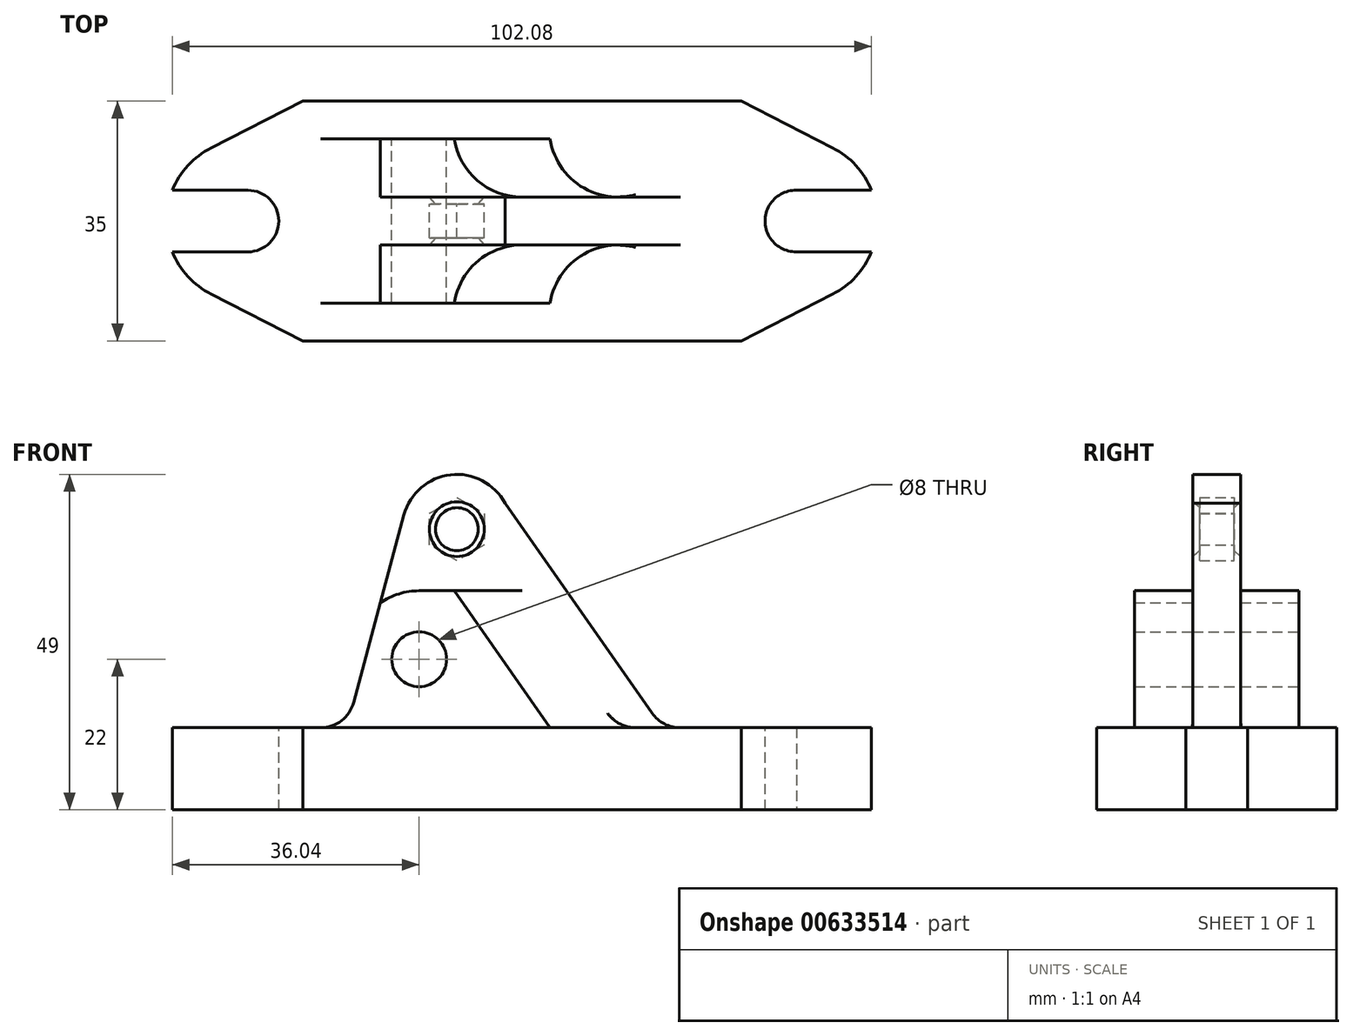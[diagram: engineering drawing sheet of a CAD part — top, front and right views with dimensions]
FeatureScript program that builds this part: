
annotation { "Feature Type Name" : "Feature", "Feature Type Description" : "" }
export const myFeature = defineFeature(function(context is Context, id is Id, definition is map)
    precondition{}
    {
        {
            var Q0;
            Q0=qCreatedBy(makeId("Front.planeOp"),FACE);
            var sketch = newSketch(context, id + "F0", { "sketchPlane" : qUnion([Q0])});
            skLineSegment(sketch, "E0.bottom", {"start": v(52, 6) * mm, "end": v(23.1, 6) * mm});
            skLineSegment(sketch, "E0.top", {"start": v(52, -6) * mm, "end": v(-52, -6) * mm});
            skLineSegment(sketch, "E0.left", {"start": v(-52, 6) * mm, "end": v(-52, -6) * mm});
            skLineSegment(sketch, "E0.right", {"start": v(52, 6) * mm, "end": v(52, -6) * mm});
            skPoint(sketch, "E0.middle", {"position": v(0, 0) * mm});
            skCircle(sketch, "E1", {"center": v(-9.5, 35) * mm, "radius": 2.75 * mm});
            skArc(sketch, "E2", {"start": v(-17.23, 37.07) * mm, "mid": v(-10.42, 42.95) * mm, "end": v(-2.45, 38.78) * mm});
            skLineSegment(sketch, "E3", {"start": v(-17.23, 37.07) * mm, "end": v(-24.56, 9.7) * mm});
            skLineSegment(sketch, "E4", {"start": v(-2.45, 38.78) * mm, "end": v(19.01, 8.13) * mm});
            skLineSegment(sketch, "E5", {"start": v(-9.5, 35) * mm, "end": v(-9.5, 6) * mm});
            skCircle(sketch, "E6", {"center": v(-15, 16) * mm, "radius": 4 * mm});
            skPoint(sketch, "E7.newPointB", {"position": v(-52, 6) * mm});
            skArc(sketch, "E7.filletArc", {"start": v(19.01, 8.13) * mm, "mid": v(20.8, 6.56) * mm, "end": v(23.1, 6) * mm});
            skLineSegment(sketch, "E8", {"start": v(-29.39, 6) * mm, "end": v(-52, 6) * mm});
            skPoint(sketch, "E9.visualSharp", {"position": v(-25.55, 6) * mm});
            skArc(sketch, "E9.filletArc", {"start": v(-29.39, 6) * mm, "mid": v(-26.35, 7.03) * mm, "end": v(-24.56, 9.7) * mm});
            skLineSegment(sketch, "E10", {"start": v(16.6, 6) * mm, "end": v(23.1, 6) * mm});
            skLineSegment(sketch, "E11", {"start": v(-9.5, 26) * mm, "end": v(3.01, 8.13) * mm});
            skArc(sketch, "E12.filletArc", {"start": v(3.01, 8.13) * mm, "mid": v(4.8, 6.56) * mm, "end": v(7.1, 6) * mm});
            skLineSegment(sketch, "E13", {"start": v(-29.39, 6) * mm, "end": v(9.04, 6) * mm});
            skLineSegment(sketch, "E14", {"start": v(-15, 16) * mm, "end": v(-15, 26) * mm});
            skLineSegment(sketch, "E15", {"start": v(-15, 26) * mm, "end": v(-9.5, 26) * mm});
            skArc(sketch, "E16", {"start": v(-15, 26) * mm, "mid": v(-17.97, 25.55) * mm, "end": v(-20.67, 24.24) * mm});
            skLineSegment(sketch, "E17", {"start": v(-15, 26) * mm, "end": v(0, 26) * mm});
            skLineSegment(sketch, "E18", {"start": v(0, 26) * mm, "end": v(12.51, 8.13) * mm});
            skArc(sketch, "E19.filletArc", {"start": v(12.51, 8.13) * mm, "mid": v(14.3, 6.56) * mm, "end": v(16.6, 6) * mm});
            skLineSegment(sketch, "E20", {"start": v(7.1, 6) * mm, "end": v(16.6, 6) * mm});
            skSolve(sketch);
        }
        {
            var Q0;
            Q0=makeQuery(id+"F0.imprint","IMPRINT",FACE,{"disambiguationData":[TD([[makeQuery(id+"F0.imprint","IMPRINT",EDGE,{"derivedFrom":sQuery(id+"F0.wireOp",EDGE,"E0.bottom")}),1.0]])]});
            extrude(context, id + "F1", {"entities" : qUnion([Q0]), "endBound" : BoundingType.SYMMETRIC, "depth" : 35 * mm, "offsetDistance" : 25 * mm});
        }
        {
            var Q0;
            Q0=makeQuery(id+"F0.imprint","IMPRINT",FACE,{"disambiguationData":[TD([[makeQuery(id+"F0.imprint","IMPRINT",EDGE,{"derivedFrom":sQuery(id+"F0.wireOp",EDGE,"E6")}),-1.0]])]});
            var Q1;
            {var subQ3=sQuery(id+"F0.wireOp",EDGE,"E11");Q1=makeQuery(id+"F0.imprint","IMPRINT",FACE,{"disambiguationData":[TD([[makeQuery(id+"F0.imprint","IMPRINT",EDGE,{"derivedFrom":subQ3}),-1.0]])]});}
            var Q2;
            {var subQ2=sQuery(id+"F0.wireOp",EDGE,"E11");Q2=makeQuery(id+"F0.imprint","IMPRINT",FACE,{"disambiguationData":[TD([[makeQuery(id+"F0.imprint","IMPRINT",EDGE,{"derivedFrom":subQ2}),1.0]])]});}
            extrude(context, id + "F2", {"entities" : qUnion([Q0, Q1, Q2]), "operationType" : NewBodyOperationType.ADD, "endBound" : BoundingType.SYMMETRIC, "depth" : 24 * mm, "offsetDistance" : 25 * mm});
        }
        {
            var Q0;
            Q0=makeQuery(id+"F0.imprint","IMPRINT",FACE,{"disambiguationData":[TD([[makeQuery(id+"F0.imprint","IMPRINT",EDGE,{"derivedFrom":sQuery(id+"F0.wireOp",EDGE,"E1")}),-1.0]])]});
            extrude(context, id + "F3", {"entities" : qUnion([Q0]), "operationType" : NewBodyOperationType.ADD, "endBound" : BoundingType.SYMMETRIC, "depth" : 7 * mm, "offsetDistance" : 25 * mm});
        }
        {
            var Q0;
            {var subQ0=sQuery(id+"F0.wireOp",EDGE,"E19.filletArc");var subQ1=sQuery(id+"F0.wireOp",EDGE,"E18");var subQ2=sQuery(id+"F0.wireOp",EDGE,"E17");var subQ3=sQuery(id+"F0.wireOp",EDGE,"E16");var subQ4=sQuery(id+"F0.wireOp",EDGE,"E3");Q0=makeQuery(id+"F3.boolean.opBoolean","SPLIT",FACE,{"disambiguationData":[TD([makeQuery(id+"F2.opExtrude","CAP_FACE",FACE,{"disambiguationData":[OSD([subQ4,sQuery(id+"F0.wireOp",EDGE,"E6"),sQuery(id+"F0.wireOp",EDGE,"E9.filletArc"),sQuery(id+"F0.wireOp",EDGE,"E13"),subQ3,subQ2,subQ1,subQ0,sQuery(id+"F0.wireOp",EDGE,"E20")])],"isStart":false})])],"derivedFrom":makeQuery(id+"F2.opExtrude","SWEPT_FACE",FACE,{"disambiguationData":[OSD([subQ2])]})});}
            var sketch = newSketch(context, id + "F4", { "sketchPlane" : qUnion([Q0])});
            skCircle(sketch, "E21", {"center": v(0, -13.5) * mm, "radius": 10 * mm});
            skSolve(sketch);
        }
        {
            var Q0;
            Q0=makeQuery(id+"F2.opExtrude","CAP_FACE",FACE,{"disambiguationData":[OSD([sQuery(id+"F0.wireOp",EDGE,"E3"),sQuery(id+"F0.wireOp",EDGE,"E6"),sQuery(id+"F0.wireOp",EDGE,"E9.filletArc"),sQuery(id+"F0.wireOp",EDGE,"E13"),sQuery(id+"F0.wireOp",EDGE,"E16"),sQuery(id+"F0.wireOp",EDGE,"E17"),sQuery(id+"F0.wireOp",EDGE,"E18"),sQuery(id+"F0.wireOp",EDGE,"E19.filletArc"),sQuery(id+"F0.wireOp",EDGE,"E20")])],"isStart":false});
            var sketch = newSketch(context, id + "F5", { "sketchPlane" : qUnion([Q0])});
            skLineSegment(sketch, "E22", {"start": v(0, 26) * mm, "end": v(14, 6) * mm});
            skSolve(sketch);
        }
        {
            var Q0;
            Q0=makeQuery(id+"F2.opExtrude","CAP_FACE",FACE,{"disambiguationData":[OSD([sQuery(id+"F0.wireOp",EDGE,"E3"),sQuery(id+"F0.wireOp",EDGE,"E6"),sQuery(id+"F0.wireOp",EDGE,"E9.filletArc"),sQuery(id+"F0.wireOp",EDGE,"E13"),sQuery(id+"F0.wireOp",EDGE,"E16"),sQuery(id+"F0.wireOp",EDGE,"E17"),sQuery(id+"F0.wireOp",EDGE,"E18"),sQuery(id+"F0.wireOp",EDGE,"E19.filletArc"),sQuery(id+"F0.wireOp",EDGE,"E20")])],"isStart":true});
            var sketch = newSketch(context, id + "F6", { "sketchPlane" : qUnion([Q0])});
            skLineSegment(sketch, "E23", {"start": v(0, 26) * mm, "end": v(-14, 6) * mm});
            skSolve(sketch);
        }
        {
            var Q0;
            {var subQ0=sQuery(id+"F0.wireOp",EDGE,"E19.filletArc");var subQ1=sQuery(id+"F0.wireOp",EDGE,"E18");var subQ2=sQuery(id+"F0.wireOp",EDGE,"E17");var subQ3=sQuery(id+"F0.wireOp",EDGE,"E16");var subQ4=sQuery(id+"F0.wireOp",EDGE,"E3");Q0=makeQuery(id+"F3.boolean.opBoolean","SPLIT",FACE,{"disambiguationData":[TD([makeQuery(id+"F2.opExtrude","CAP_FACE",FACE,{"disambiguationData":[OSD([subQ4,sQuery(id+"F0.wireOp",EDGE,"E6"),sQuery(id+"F0.wireOp",EDGE,"E9.filletArc"),sQuery(id+"F0.wireOp",EDGE,"E13"),subQ3,subQ2,subQ1,subQ0,sQuery(id+"F0.wireOp",EDGE,"E20")])],"isStart":true})])],"derivedFrom":makeQuery(id+"F2.opExtrude","SWEPT_FACE",FACE,{"disambiguationData":[OSD([subQ2])]})});}
            var sketch = newSketch(context, id + "F7", { "sketchPlane" : qUnion([Q0])});
            skCircle(sketch, "E24", {"center": v(0, 13.5) * mm, "radius": 10 * mm});
            skSolve(sketch);
        }
        {
            var Q0;
            Q0=qSketchRegion(id+"F4",true);
            var Q1;
            Q1=sQuery(id+"F5.wireOp",EDGE,"E22");
            sweep(context, id + "F8", {"operationType" : NewBodyOperationType.REMOVE, "profiles" : qUnion([Q0]), "path" : qUnion([Q1])});
        }
        {
            var Q0;
            Q0=qSketchRegion(id+"F7",true);
            var Q1;
            Q1=sQuery(id+"F6.wireOp",EDGE,"E23");
            sweep(context, id + "F9", {"operationType" : NewBodyOperationType.REMOVE, "profiles" : qUnion([Q0]), "path" : qUnion([Q1])});
        }
        {
            var Q0;
            Q0=makeQuery(id+"F9.boolean.opBoolean","MERGE",FACE,{"derivedFrom":[makeQuery(id+"F8.boolean.opBoolean","MERGE",FACE,{"derivedFrom":[makeQuery(id+"F1.opExtrude","SWEPT_FACE",FACE,{"disambiguationData":[OSD([sQuery(id+"F0.wireOp",EDGE,"E0.bottom"),sQuery(id+"F0.wireOp",EDGE,"E8"),sQuery(id+"F0.wireOp",EDGE,"E10"),sQuery(id+"F0.wireOp",EDGE,"E13"),sQuery(id+"F0.wireOp",EDGE,"E20")])]}),makeQuery(id+"F8.opSweep","CAP_FACE",FACE,{"disambiguationData":[OSD([sQuery(id+"F4.wireOp",EDGE,"E21"),sQuery(id+"F5.wireOp",VERTEX,"E22.end")])],"isStart":false})]}),makeQuery(id+"F9.opSweep","CAP_FACE",FACE,{"disambiguationData":[OSD([sQuery(id+"F6.wireOp",VERTEX,"E23.end"),sQuery(id+"F7.wireOp",EDGE,"E24")])],"isStart":false})]});
            var sketch = newSketch(context, id + "F10", { "sketchPlane" : qUnion([Q0])});
            skCircle(sketch, "E25", {"center": v(40, 0) * mm, "radius": 4.5 * mm});
            skSolve(sketch);
        }
        {
            var Q0;
            Q0=sQuery(id+"F10.wireOp",VERTEX,"E25.center");
            var Q1;
            Q1=makeQuery(id+"F1.opExtrude","SWEPT_BODY",BODY,{"disambiguationData":[OSD([sQuery(id+"F0.wireOp",EDGE,"E0.bottom"),sQuery(id+"F0.wireOp",EDGE,"E0.top"),sQuery(id+"F0.wireOp",EDGE,"E0.left"),sQuery(id+"F0.wireOp",EDGE,"E0.right"),sQuery(id+"F0.wireOp",EDGE,"E8"),sQuery(id+"F0.wireOp",EDGE,"E10"),sQuery(id+"F0.wireOp",EDGE,"E13"),sQuery(id+"F0.wireOp",EDGE,"E20")])]});
            hole(context, id + "F11", {"style" : HoleStyle.SIMPLE, "endStyle" : HoleEndStyle.THROUGH, "holeDiameter" : 9 * mm, "isTappedThrough" : true, "tappedDepth" : 12 * mm, "tapClearance" : 3, "startFromSketch" : true, "locations" : qUnion([Q0]), "scope" : qUnion([Q1])});
        }
        {
            var Q0;
            Q0=makeQuery(id+"F9.boolean.opBoolean","MERGE",FACE,{"derivedFrom":[makeQuery(id+"F8.boolean.opBoolean","MERGE",FACE,{"derivedFrom":[makeQuery(id+"F1.opExtrude","SWEPT_FACE",FACE,{"disambiguationData":[OSD([sQuery(id+"F0.wireOp",EDGE,"E0.bottom"),sQuery(id+"F0.wireOp",EDGE,"E8"),sQuery(id+"F0.wireOp",EDGE,"E10"),sQuery(id+"F0.wireOp",EDGE,"E13"),sQuery(id+"F0.wireOp",EDGE,"E20")])]}),makeQuery(id+"F8.opSweep","CAP_FACE",FACE,{"disambiguationData":[OSD([sQuery(id+"F4.wireOp",EDGE,"E21"),sQuery(id+"F5.wireOp",VERTEX,"E22.end")])],"isStart":false})]}),makeQuery(id+"F9.opSweep","CAP_FACE",FACE,{"disambiguationData":[OSD([sQuery(id+"F6.wireOp",VERTEX,"E23.end"),sQuery(id+"F7.wireOp",EDGE,"E24")])],"isStart":false})]});
            var sketch = newSketch(context, id + "F12", { "sketchPlane" : qUnion([Q0])});
            skCircle(sketch, "E26", {"center": v(-40, 0) * mm, "radius": 4.5 * mm});
            skLineSegment(sketch, "E27", {"start": v(-40, 4.5) * mm, "end": v(-52, 4.5) * mm});
            skLineSegment(sketch, "E28", {"start": v(-40, -4.5) * mm, "end": v(-52, -4.5) * mm});
            skLineSegment(sketch, "E29", {"start": v(32, -17.5) * mm, "end": v(32, 17.5) * mm});
            skLineSegment(sketch, "E30", {"start": v(32, -17.5) * mm, "end": v(45.36, -10.7) * mm});
            skLineSegment(sketch, "E31", {"start": v(45.36, 10.7) * mm, "end": v(32, 17.5) * mm});
            skPoint(sketch, "E32.visualSharp", {"position": v(66.35, 0) * mm});
            skArc(sketch, "E32.filletArc", {"start": v(45.36, -10.7) * mm, "mid": v(51.91, 0) * mm, "end": v(45.36, 10.7) * mm});
            skLineSegment(sketch, "E33", {"start": v(39.91, -4.5) * mm, "end": v(52, -4.5) * mm});
            skLineSegment(sketch, "E34", {"start": v(39.91, 4.5) * mm, "end": v(52, 4.5) * mm});
            skSolve(sketch);
        }
        {
            var Q0;
            Q0=sQuery(id+"F12.wireOp",VERTEX,"E26.center");
            var Q1;
            Q1=makeQuery(id+"F1.opExtrude","SWEPT_BODY",BODY,{"disambiguationData":[OSD([sQuery(id+"F0.wireOp",EDGE,"E0.bottom"),sQuery(id+"F0.wireOp",EDGE,"E0.top"),sQuery(id+"F0.wireOp",EDGE,"E0.left"),sQuery(id+"F0.wireOp",EDGE,"E0.right"),sQuery(id+"F0.wireOp",EDGE,"E8"),sQuery(id+"F0.wireOp",EDGE,"E10"),sQuery(id+"F0.wireOp",EDGE,"E13"),sQuery(id+"F0.wireOp",EDGE,"E20")])]});
            hole(context, id + "F13", {"style" : HoleStyle.SIMPLE, "endStyle" : HoleEndStyle.THROUGH, "holeDiameter" : 9 * mm, "isTappedThrough" : true, "tappedDepth" : 12 * mm, "tapClearance" : 3, "startFromSketch" : true, "locations" : qUnion([Q0]), "scope" : qUnion([Q1])});
        }
        {
            var Q0;
            Q0=makeQuery(id+"F9.boolean.opBoolean","MERGE",FACE,{"derivedFrom":[makeQuery(id+"F8.boolean.opBoolean","MERGE",FACE,{"derivedFrom":[makeQuery(id+"F1.opExtrude","SWEPT_FACE",FACE,{"disambiguationData":[OSD([sQuery(id+"F0.wireOp",EDGE,"E0.bottom"),sQuery(id+"F0.wireOp",EDGE,"E8"),sQuery(id+"F0.wireOp",EDGE,"E10"),sQuery(id+"F0.wireOp",EDGE,"E13"),sQuery(id+"F0.wireOp",EDGE,"E20")])]}),makeQuery(id+"F8.opSweep","CAP_FACE",FACE,{"disambiguationData":[OSD([sQuery(id+"F4.wireOp",EDGE,"E21"),sQuery(id+"F5.wireOp",VERTEX,"E22.end")])],"isStart":false})]}),makeQuery(id+"F9.opSweep","CAP_FACE",FACE,{"disambiguationData":[OSD([sQuery(id+"F6.wireOp",VERTEX,"E23.end"),sQuery(id+"F7.wireOp",EDGE,"E24")])],"isStart":false})]});
            var sketch = newSketch(context, id + "F14", { "sketchPlane" : qUnion([Q0])});
            skLineSegment(sketch, "E35", {"start": v(-32, 17.5) * mm, "end": v(-32, -17.5) * mm});
            skLineSegment(sketch, "E36", {"start": v(-32, 17.5) * mm, "end": v(-45.36, 10.7) * mm});
            skPoint(sketch, "E36.endSnap0", {"position": v(-52, 0) * mm});
            skLineSegment(sketch, "E37", {"start": v(-45.36, -10.7) * mm, "end": v(-32, -17.5) * mm});
            skPoint(sketch, "E38.visualSharp", {"position": v(-66.35, 0) * mm});
            skArc(sketch, "E38.filletArc", {"start": v(-45.36, 10.7) * mm, "mid": v(-51.91, 0) * mm, "end": v(-45.36, -10.7) * mm});
            skSolve(sketch);
        }
        {
            var Q0;
            {var subQ3=sQuery(id+"F14.wireOp",EDGE,"E36");Q0=makeQuery(id+"F14.imprint","IMPRINT",FACE,{"disambiguationData":[TD([[makeQuery(id+"F14.imprint","IMPRINT",EDGE,{"derivedFrom":subQ3}),-1.0]])]});}
            var Q1;
            Q1=makeQuery(id+"F1.opExtrude","CAP_EDGE",EDGE,{"disambiguationData":[OSD([sQuery(id+"F0.wireOp",EDGE,"E0.left")])],"isStart":false});
            sweep(context, id + "F15", {"operationType" : NewBodyOperationType.REMOVE, "profiles" : qUnion([Q0]), "path" : qUnion([Q1])});
        }
        {
            var Q0;
            {var subQ0=sQuery(id+"F12.wireOp",EDGE,"E27");Q0=makeQuery(id+"F12.imprint","IMPRINT",FACE,{"disambiguationData":[TD([[makeQuery(id+"F12.imprint","IMPRINT",EDGE,{"derivedFrom":subQ0}),1.0]])]});}
            var Q1;
            Q1=sQuery(id+"F0.wireOp",EDGE,"E0.left");
            sweep(context, id + "F16", {"operationType" : NewBodyOperationType.REMOVE, "profiles" : qUnion([Q0]), "path" : qUnion([Q1])});
        }
        {
            var Q0;
            {var subQ3=sQuery(id+"F12.wireOp",EDGE,"E30");Q0=makeQuery(id+"F12.imprint","IMPRINT",FACE,{"disambiguationData":[TD([[makeQuery(id+"F12.imprint","IMPRINT",EDGE,{"derivedFrom":subQ3}),-1.0]])]});}
            var Q1;
            Q1=makeQuery(id+"F1.opExtrude","CAP_EDGE",EDGE,{"disambiguationData":[OSD([sQuery(id+"F0.wireOp",EDGE,"E0.right")])],"isStart":true});
            sweep(context, id + "F17", {"operationType" : NewBodyOperationType.REMOVE, "profiles" : qUnion([Q0]), "path" : qUnion([Q1])});
        }
        {
            var Q0;
            {var subQ0=sQuery(id+"F12.wireOp",EDGE,"E33");var subQ1=sQuery(id+"F12.wireOp",EDGE,"E32.filletArc");var subQ2=makeQuery(id+"F12.imprint","INTERSECT",VERTEX,{"derivedFrom":[subQ1,subQ0]});Q0=makeQuery(id+"F12.imprint","IMPRINT",FACE,{"disambiguationData":[TD([[makeQuery(id+"F12.imprint","IMPRINT",EDGE,{"disambiguationData":[TD([[subQ2,-1.0]])],"derivedFrom":subQ1}),1.0]])]});}
            var Q1;
            {var subQ0=sQuery(id+"F12.wireOp",EDGE,"E33");var subQ1=sQuery(id+"F12.wireOp",EDGE,"E32.filletArc");var subQ2=makeQuery(id+"F12.imprint","INTERSECT",VERTEX,{"derivedFrom":[subQ1,subQ0]});Q1=makeQuery(id+"F12.imprint","IMPRINT",FACE,{"disambiguationData":[TD([[makeQuery(id+"F12.imprint","IMPRINT",EDGE,{"disambiguationData":[TD([[subQ2,-1.0]])],"derivedFrom":subQ1}),-1.0]])]});}
            var Q2;
            {var subQ8=sQuery(id+"F12.wireOp",EDGE,"E31");Q2=makeQuery(id+"F12.imprint","IMPRINT",FACE,{"disambiguationData":[TD([[makeQuery(id+"F12.imprint","IMPRINT",EDGE,{"derivedFrom":subQ8}),-1.0]])]});}
            var Q3;
            Q3=makeQuery(id+"F1.opExtrude","CAP_EDGE",EDGE,{"disambiguationData":[OSD([sQuery(id+"F0.wireOp",EDGE,"E0.right")])],"isStart":true});
            sweep(context, id + "F18", {"operationType" : NewBodyOperationType.REMOVE, "profiles" : qUnion([Q0, Q1, Q2]), "path" : qUnion([Q3])});
        }
        {
            var Q0;
            Q0=makeQuery(id+"F3.opExtrude","CAP_FACE",FACE,{"disambiguationData":[OSD([sQuery(id+"F0.wireOp",EDGE,"E1"),sQuery(id+"F0.wireOp",EDGE,"E2"),sQuery(id+"F0.wireOp",EDGE,"E3"),sQuery(id+"F0.wireOp",EDGE,"E4"),sQuery(id+"F0.wireOp",EDGE,"E7.filletArc"),sQuery(id+"F0.wireOp",EDGE,"E10"),sQuery(id+"F0.wireOp",EDGE,"E16"),sQuery(id+"F0.wireOp",EDGE,"E17"),sQuery(id+"F0.wireOp",EDGE,"E18"),sQuery(id+"F0.wireOp",EDGE,"E19.filletArc")])],"isStart":false});
            var sketch = newSketch(context, id + "F19", { "sketchPlane" : qUnion([Q0])});
            skPoint(sketch, "E39", {"position": v(-9.5, 35) * mm});
            skSolve(sketch);
        }
        {
            var Q0;
            Q0=sQuery(id+"F19.wireOp",VERTEX,"E39");
            var Q1;
            Q1=makeQuery(id+"F1.opExtrude","SWEPT_BODY",BODY,{"disambiguationData":[OSD([sQuery(id+"F0.wireOp",EDGE,"E0.bottom"),sQuery(id+"F0.wireOp",EDGE,"E0.top"),sQuery(id+"F0.wireOp",EDGE,"E0.left"),sQuery(id+"F0.wireOp",EDGE,"E0.right"),sQuery(id+"F0.wireOp",EDGE,"E8"),sQuery(id+"F0.wireOp",EDGE,"E10"),sQuery(id+"F0.wireOp",EDGE,"E13"),sQuery(id+"F0.wireOp",EDGE,"E20")])]});
            hole(context, id + "F20", {"style" : HoleStyle.C_SINK, "endStyle" : HoleEndStyle.BLIND, "holeDiameter" : 5.5 * mm, "cSinkDiameter" : 8 * mm, "cSinkAngle" : 82 * degree, "holeDepth" : 3.5 * mm, "isTappedThrough" : true, "tappedDepth" : 12 * mm, "tapClearance" : 3, "startFromSketch" : true, "locations" : qUnion([Q0]), "scope" : qUnion([Q1])});
        }
        {
            var Q0;
            Q0=makeQuery(id+"F3.opExtrude","CAP_FACE",FACE,{"disambiguationData":[OSD([sQuery(id+"F0.wireOp",EDGE,"E1"),sQuery(id+"F0.wireOp",EDGE,"E2"),sQuery(id+"F0.wireOp",EDGE,"E3"),sQuery(id+"F0.wireOp",EDGE,"E4"),sQuery(id+"F0.wireOp",EDGE,"E7.filletArc"),sQuery(id+"F0.wireOp",EDGE,"E10"),sQuery(id+"F0.wireOp",EDGE,"E16"),sQuery(id+"F0.wireOp",EDGE,"E17"),sQuery(id+"F0.wireOp",EDGE,"E18"),sQuery(id+"F0.wireOp",EDGE,"E19.filletArc")])],"isStart":true});
            var sketch = newSketch(context, id + "F21", { "sketchPlane" : qUnion([Q0])});
            skPoint(sketch, "E40", {"position": v(9.5, 35) * mm});
            skSolve(sketch);
        }
        {
            var Q0;
            Q0=sQuery(id+"F21.wireOp",VERTEX,"E40");
            var Q1;
            Q1=makeQuery(id+"F1.opExtrude","SWEPT_BODY",BODY,{"disambiguationData":[OSD([sQuery(id+"F0.wireOp",EDGE,"E0.bottom"),sQuery(id+"F0.wireOp",EDGE,"E0.top"),sQuery(id+"F0.wireOp",EDGE,"E0.left"),sQuery(id+"F0.wireOp",EDGE,"E0.right"),sQuery(id+"F0.wireOp",EDGE,"E8"),sQuery(id+"F0.wireOp",EDGE,"E10"),sQuery(id+"F0.wireOp",EDGE,"E13"),sQuery(id+"F0.wireOp",EDGE,"E20")])]});
            hole(context, id + "F22", {"style" : HoleStyle.C_SINK, "endStyle" : HoleEndStyle.BLIND, "holeDiameter" : 5.5 * mm, "cSinkDiameter" : 8 * mm, "cSinkAngle" : 82 * degree, "holeDepth" : 3.5 * mm, "isTappedThrough" : true, "tappedDepth" : 12 * mm, "tapClearance" : 3, "startFromSketch" : true, "locations" : qUnion([Q0]), "scope" : qUnion([Q1])});
        }
        {
            var Q0;
            Q0=qCreatedBy(makeId("Front.planeOp"),FACE);
            var sketch = newSketch(context, id + "F23", { "sketchPlane" : qUnion([Q0])});
            skCircle(sketch, "E41.cCircle", {"center": v(-9.5, 35) * mm, "radius": 3.99 * mm, "construction": true});
            skLineSegment(sketch, "E41.0", {"start": v(-9.51, 30.4) * mm, "end": v(-13.5, 32.7) * mm});
            skLineSegment(sketch, "E41.1", {"start": v(-13.5, 32.7) * mm, "end": v(-13.48, 37.31) * mm});
            skLineSegment(sketch, "E41.2", {"start": v(-13.48, 37.31) * mm, "end": v(-9.49, 39.6) * mm});
            skLineSegment(sketch, "E41.3", {"start": v(-9.49, 39.6) * mm, "end": v(-5.5, 37.29) * mm});
            skLineSegment(sketch, "E41.4", {"start": v(-5.5, 37.29) * mm, "end": v(-5.52, 32.68) * mm});
            skLineSegment(sketch, "E41.5", {"start": v(-5.52, 32.68) * mm, "end": v(-9.51, 30.4) * mm});
            skPoint(sketch, "E41.0.midPoint", {"position": v(-11.5, 31.55) * mm});
            skSolve(sketch);
        }
        {
            var Q0;
            Q0=qSketchRegion(id+"F23",true);
            extrude(context, id + "F24", {"entities" : qUnion([Q0]), "operationType" : NewBodyOperationType.REMOVE, "endBound" : BoundingType.SYMMETRIC, "depth" : 5 * mm, "offsetDistance" : 25 * mm});
        }
    });
